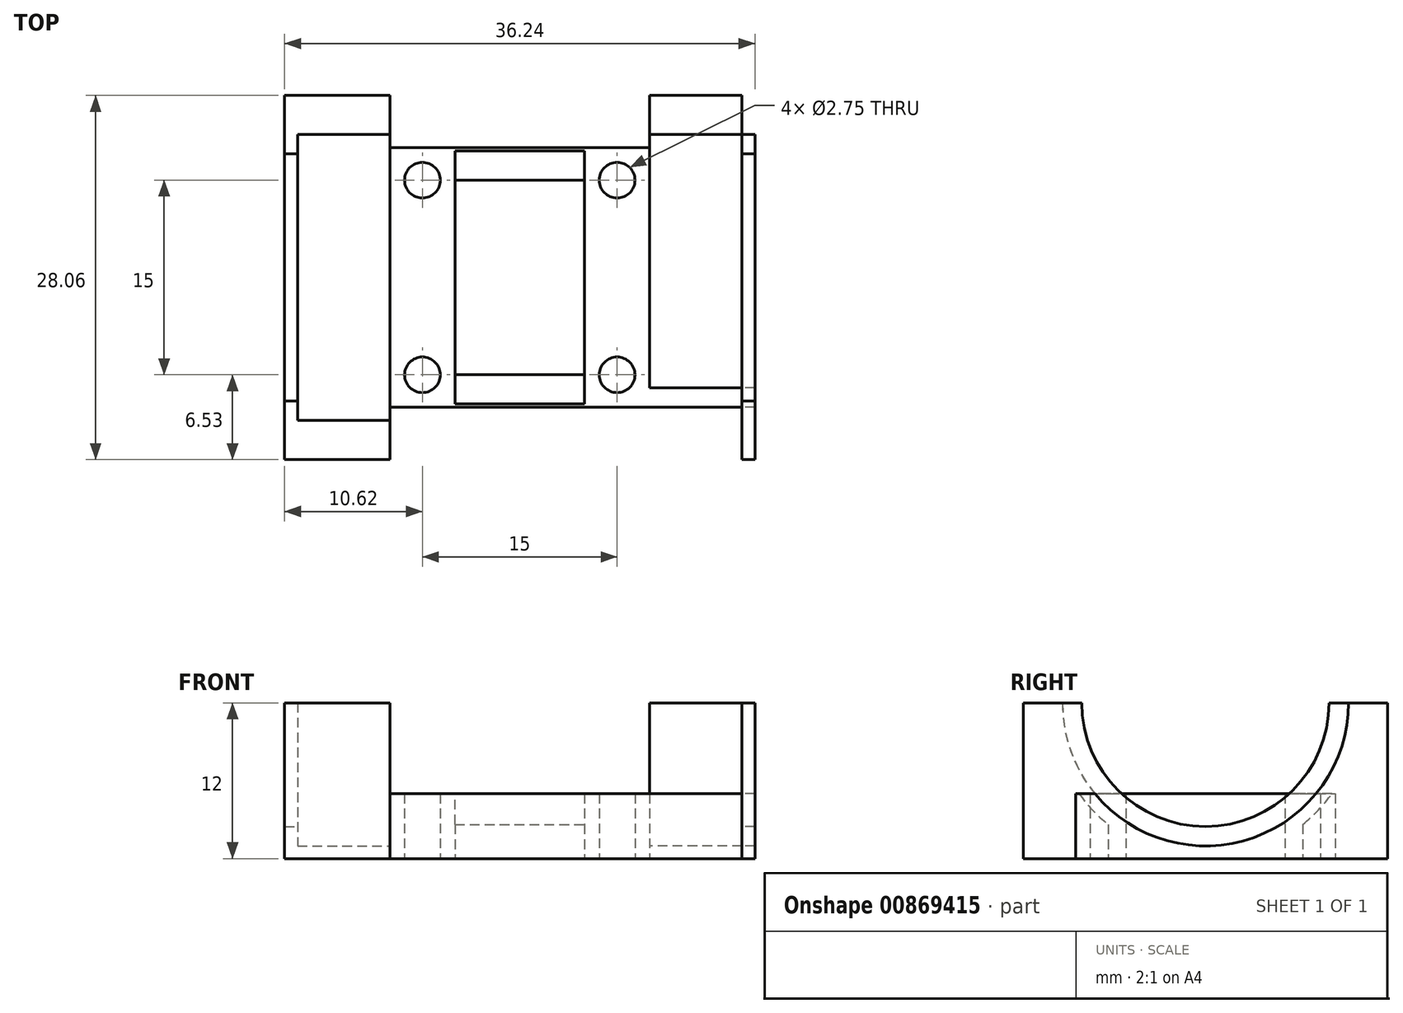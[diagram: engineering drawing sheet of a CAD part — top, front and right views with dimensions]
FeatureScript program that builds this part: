
annotation { "Feature Type Name" : "Feature", "Feature Type Description" : "" }
export const myFeature = defineFeature(function(context is Context, id is Id, definition is map)
    precondition{}
    {
        {
            var Q0;
            Q0=qCreatedBy(makeId("Top.planeOp"),FACE);
            var sketch = newSketch(context, id + "F0", { "sketchPlane" : qUnion([Q0])});
            skLineSegment(sketch, "E0.bottom", {"start": v(0, 0) * mm, "end": v(20, 0) * mm});
            skLineSegment(sketch, "E0.top", {"start": v(0, 20) * mm, "end": v(20, 20) * mm});
            skLineSegment(sketch, "E0.left", {"start": v(0, 0) * mm, "end": v(0, 20) * mm});
            skLineSegment(sketch, "E0.right", {"start": v(20, 0) * mm, "end": v(20, 20) * mm});
            skLineSegment(sketch, "E1", {"start": v(0, 10) * mm, "end": v(20, 10) * mm, "construction": true});
            skLineSegment(sketch, "E2", {"start": v(10, 20) * mm, "end": v(10, 0) * mm, "construction": true});
            skCircle(sketch, "E3", {"center": v(2.5, 2.5) * mm, "radius": 1.38 * mm});
            skCircle(sketch, "E4.MirrorC", {"center": v(2.5, 17.5) * mm, "radius": 1.38 * mm});
            skCircle(sketch, "E5.MirrorC", {"center": v(17.5, 17.5) * mm, "radius": 1.38 * mm});
            skCircle(sketch, "E6.MirrorC", {"center": v(17.5, 2.5) * mm, "radius": 1.38 * mm});
            skLineSegment(sketch, "E7.bottom", {"start": v(5, 17.5) * mm, "end": v(15, 17.5) * mm});
            skLineSegment(sketch, "E7.top", {"start": v(5, 2.5) * mm, "end": v(15, 2.5) * mm});
            skLineSegment(sketch, "E7.left", {"start": v(5, 17.5) * mm, "end": v(5, 2.5) * mm});
            skLineSegment(sketch, "E7.right", {"start": v(15, 17.5) * mm, "end": v(15, 2.5) * mm});
            skSolve(sketch);
        }
        {
            var Q0;
            Q0=makeQuery(id+"F0.imprint","IMPRINT",FACE,{"disambiguationData":[TD([[makeQuery(id+"F0.imprint","IMPRINT",EDGE,{"derivedFrom":sQuery(id+"F0.wireOp",EDGE,"E0.bottom")}),1.0]])]});
            extrude(context, id + "F1", {"entities" : qUnion([Q0]), "depth" : 5 * mm, "offsetDistance" : 25 * mm});
        }
        {
            var Q0;
            Q0=makeQuery(id+"F1.opExtrude","SWEPT_FACE",FACE,{"disambiguationData":[OSD([sQuery(id+"F0.wireOp",EDGE,"E0.left")])]});
            var sketch = newSketch(context, id + "F2", { "sketchPlane" : qUnion([Q0])});
            skArc(sketch, "E8", {"start": v(-21.03, 12) * mm, "mid": v(-10, 0.97) * mm, "end": v(1.02, 12) * mm});
            skPoint(sketch, "E8.centerSnap0", {"position": v(-10, 5) * mm});
            skLineSegment(sketch, "E9", {"start": v(-21.03, 12) * mm, "end": v(-24.02, 12) * mm});
            skLineSegment(sketch, "E10", {"start": v(-24.02, 12) * mm, "end": v(-24.02, 0) * mm});
            skLineSegment(sketch, "E11", {"start": v(-24.02, 0) * mm, "end": v(4.02, 0) * mm});
            skLineSegment(sketch, "E12", {"start": v(4.02, 0) * mm, "end": v(4.02, 12) * mm});
            skLineSegment(sketch, "E13", {"start": v(4.02, 12) * mm, "end": v(1.02, 12) * mm});
            skLineSegment(sketch, "E14", {"start": v(-10, 12) * mm, "end": v(-10, 0) * mm, "construction": true});
            skSolve(sketch);
        }
        {
            var Q0;
            {var subQ1=sQuery(id+"F2.wireOp",EDGE,"E9");Q0=makeQuery(id+"F2.imprint","IMPRINT",FACE,{"disambiguationData":[TD([[makeQuery(id+"F2.imprint","IMPRINT",EDGE,{"derivedFrom":subQ1}),1.0]])]});}
            var Q1;
            {var subQ0=sQuery(id+"F0.wireOp",EDGE,"E0.left");var subQ1=makeQuery(id+"F1.opExtrude","SWEPT_EDGE",EDGE,{"disambiguationData":[OSD([sQuery(id+"F0.wireOp",EDGE,"E0.bottom"),subQ0])]});Q1=makeQuery(id+"F2.imprint","IMPRINT",FACE,{"disambiguationData":[TD([[makeQuery(id+"F2.imprint","IMPRINT",EDGE,{"derivedFrom":subQ1}),-1.0]])]});}
            var Q2;
            {var subQ1=sQuery(id+"F2.wireOp",EDGE,"E12");Q2=makeQuery(id+"F2.imprint","IMPRINT",FACE,{"disambiguationData":[TD([[makeQuery(id+"F2.imprint","IMPRINT",EDGE,{"derivedFrom":subQ1}),1.0]])]});}
            extrude(context, id + "F3", {"entities" : qUnion([Q0, Q1, Q2]), "operationType" : NewBodyOperationType.ADD, "depth" : 7.12 * mm, "offsetDistance" : 25 * mm});
        }
        {
            var Q0;
            Q0=qCreatedBy(makeId("Right.planeOp"),FACE);
            cPlane(context, id + "F4", {"entities" : qUnion([Q0]), "cplaneType" : CPlaneType.OFFSET, "offset" : 10 * mm, "width" : 150 * mm, "height" : 150 * mm});
        }
        {
            var Q0;
            Q0=makeQuery(id+"F1.opExtrude","SWEPT_FACE",FACE,{"disambiguationData":[OSD([sQuery(id+"F0.wireOp",EDGE,"E0.right")])]});
            var sketch = newSketch(context, id + "F5", { "sketchPlane" : qUnion([Q0])});
            skArc(sketch, "E15.0", {"start": v(1.48, 5) * mm, "mid": v(-0.38, 8.28) * mm, "end": v(-1.02, 12) * mm});
            skLineSegment(sketch, "E16.0", {"start": v(-4.02, 12) * mm, "end": v(-1.02, 12) * mm});
            skLineSegment(sketch, "E17.0", {"start": v(-4.02, 0) * mm, "end": v(-4.02, 12) * mm});
            skLineSegment(sketch, "E18.0", {"start": v(0, 0) * mm, "end": v(-4.02, 0) * mm});
            skLineSegment(sketch, "E19.0", {"start": v(0, 0) * mm, "end": v(20, 0) * mm});
            skLineSegment(sketch, "E20.0", {"start": v(24.02, 0) * mm, "end": v(20, 0) * mm});
            skLineSegment(sketch, "E21.0", {"start": v(24.02, 12) * mm, "end": v(24.02, 0) * mm});
            skLineSegment(sketch, "E22.0", {"start": v(21.03, 12) * mm, "end": v(24.02, 12) * mm});
            skArc(sketch, "E23.0", {"start": v(21.03, 12) * mm, "mid": v(20.38, 8.28) * mm, "end": v(18.52, 5) * mm});
            skArc(sketch, "E24.0", {"start": v(18.52, 5) * mm, "mid": v(10, 0.97) * mm, "end": v(1.48, 5) * mm});
            skSolve(sketch);
        }
        {
            var Q0;
            {var subQ3=sQuery(id+"F5.wireOp",EDGE,"E15.0");Q0=makeQuery(id+"F5.imprint","IMPRINT",FACE,{"disambiguationData":[TD([[makeQuery(id+"F5.imprint","IMPRINT",EDGE,{"derivedFrom":subQ3}),1.0]])]});}
            var Q1;
            Q1=makeQuery(id+"F5.imprint","IMPRINT",FACE,{"disambiguationData":[TD([[makeQuery(id+"F5.imprint","IMPRINT",EDGE,{"derivedFrom":sQuery(id+"F5.wireOp",EDGE,"E19.0")}),1.0]])]});
            var Q2;
            Q2=makeQuery(id+"F5.imprint","IMPRINT",FACE,{"disambiguationData":[TD([[makeQuery(id+"F5.imprint","IMPRINT",EDGE,{"derivedFrom":sQuery(id+"F5.wireOp",EDGE,"E20.0")}),-1.0]])]});
            extrude(context, id + "F6", {"entities" : qUnion([Q0, Q1, Q2]), "operationType" : NewBodyOperationType.ADD, "depth" : 7.12 * mm, "offsetDistance" : 25 * mm});
        }
        {
            var Q0;
            Q0=makeQuery(id+"F6.opExtrude","CAP_FACE",FACE,{"disambiguationData":[OSD([sQuery(id+"F5.wireOp",EDGE,"E15.0"),sQuery(id+"F5.wireOp",EDGE,"E16.0"),sQuery(id+"F5.wireOp",EDGE,"E17.0"),sQuery(id+"F5.wireOp",EDGE,"E18.0"),sQuery(id+"F5.wireOp",EDGE,"E19.0"),sQuery(id+"F5.wireOp",EDGE,"E20.0"),sQuery(id+"F5.wireOp",EDGE,"E21.0"),sQuery(id+"F5.wireOp",EDGE,"E22.0"),sQuery(id+"F5.wireOp",EDGE,"E23.0"),sQuery(id+"F5.wireOp",EDGE,"E24.0")])],"isStart":false});
            var sketch = newSketch(context, id + "F7", { "sketchPlane" : qUnion([Q0])});
            skLineSegment(sketch, "E25.0", {"start": v(-4.02, 0) * mm, "end": v(-4.02, 12) * mm});
            skLineSegment(sketch, "E26.0", {"start": v(24.02, 0) * mm, "end": v(-4.02, 0) * mm});
            skLineSegment(sketch, "E27.0", {"start": v(24.02, 12) * mm, "end": v(24.02, 0) * mm});
            skArc(sketch, "E28.0", {"start": v(19.53, 12) * mm, "mid": v(10, 2.47) * mm, "end": v(0.48, 12) * mm});
            skLineSegment(sketch, "E29", {"start": v(-4.02, 12) * mm, "end": v(0.48, 12) * mm});
            skLineSegment(sketch, "E30.trimOffspring", {"start": v(19.53, 12) * mm, "end": v(24.02, 12) * mm});
            skSolve(sketch);
        }
        {
            var Q0;
            {var subQ0=sQuery(id+"F7.wireOp",EDGE,"E28.0");Q0=makeQuery(id+"F7.imprint","IMPRINT",FACE,{"disambiguationData":[TD([[makeQuery(id+"F7.imprint","IMPRINT",EDGE,{"derivedFrom":subQ0}),1.0]])]});}
            var Q1;
            {var subQ3=sQuery(id+"F7.wireOp",EDGE,"E25.0");Q1=makeQuery(id+"F7.imprint","IMPRINT",FACE,{"disambiguationData":[TD([[makeQuery(id+"F7.imprint","IMPRINT",EDGE,{"derivedFrom":subQ3}),-1.0]])]});}
            extrude(context, id + "F8", {"entities" : qUnion([Q0, Q1]), "operationType" : NewBodyOperationType.ADD, "depth" : 1 * mm, "offsetDistance" : 25 * mm});
        }
        {
            var Q0;
            Q0=makeQuery(id+"F3.opExtrude","CAP_FACE",FACE,{"disambiguationData":[OSD([sQuery(id+"F2.wireOp",EDGE,"E8"),sQuery(id+"F2.wireOp",EDGE,"E9"),sQuery(id+"F2.wireOp",EDGE,"E10"),sQuery(id+"F2.wireOp",EDGE,"E11"),sQuery(id+"F2.wireOp",EDGE,"E12"),sQuery(id+"F2.wireOp",EDGE,"E13")])],"isStart":false});
            var sketch = newSketch(context, id + "F9", { "sketchPlane" : qUnion([Q0])});
            skLineSegment(sketch, "E31.0", {"start": v(-24.02, 12) * mm, "end": v(-24.02, 0) * mm});
            skLineSegment(sketch, "E32.0", {"start": v(4.02, 0) * mm, "end": v(4.02, 12) * mm});
            skLineSegment(sketch, "E33.0", {"start": v(-24.02, 0) * mm, "end": v(4.02, 0) * mm});
            skArc(sketch, "E34.0", {"start": v(-19.53, 12) * mm, "mid": v(-10, 2.47) * mm, "end": v(-0.48, 12) * mm});
            skLineSegment(sketch, "E35.0", {"start": v(-19.53, 12) * mm, "end": v(-24.02, 12) * mm});
            skLineSegment(sketch, "E36.0", {"start": v(4.02, 12) * mm, "end": v(-0.48, 12) * mm});
            skSolve(sketch);
        }
        {
            var Q0;
            {var subQ0=sQuery(id+"F9.wireOp",EDGE,"E34.0");Q0=makeQuery(id+"F9.imprint","IMPRINT",FACE,{"disambiguationData":[TD([[makeQuery(id+"F9.imprint","IMPRINT",EDGE,{"derivedFrom":subQ0}),-1.0]])]});}
            var Q1;
            {var subQ2=sQuery(id+"F9.wireOp",EDGE,"E31.0");Q1=makeQuery(id+"F9.imprint","IMPRINT",FACE,{"disambiguationData":[TD([[makeQuery(id+"F9.imprint","IMPRINT",EDGE,{"derivedFrom":subQ2}),1.0]])]});}
            extrude(context, id + "F10", {"entities" : qUnion([Q0, Q1]), "operationType" : NewBodyOperationType.ADD, "depth" : 1 * mm, "offsetDistance" : 25 * mm});
        }
        {
            var Q0;
            Q0=qCreatedBy(id+"F4.planeOp",FACE);
            var sketch = newSketch(context, id + "F11", { "sketchPlane" : qUnion([Q0])});
            skCircle(sketch, "E37", {"center": v(10, 12) * mm, "radius": 12 * mm});
            skSolve(sketch);
        }
        {
            var Q0;
            Q0=makeQuery(id+"F11.imprint","IMPRINT",FACE,{"disambiguationData":[TD([[makeQuery(id+"F11.imprint","IMPRINT",EDGE,{"derivedFrom":sQuery(id+"F11.wireOp",EDGE,"E37")}),1.0]])]});
            extrude(context, id + "F12", {"entities" : qUnion([Q0]), "operationType" : NewBodyOperationType.REMOVE, "endBound" : BoundingType.SYMMETRIC, "oppositeDirection" : true, "depth" : 10 * mm, "offsetDistance" : 25 * mm});
        }
    });
